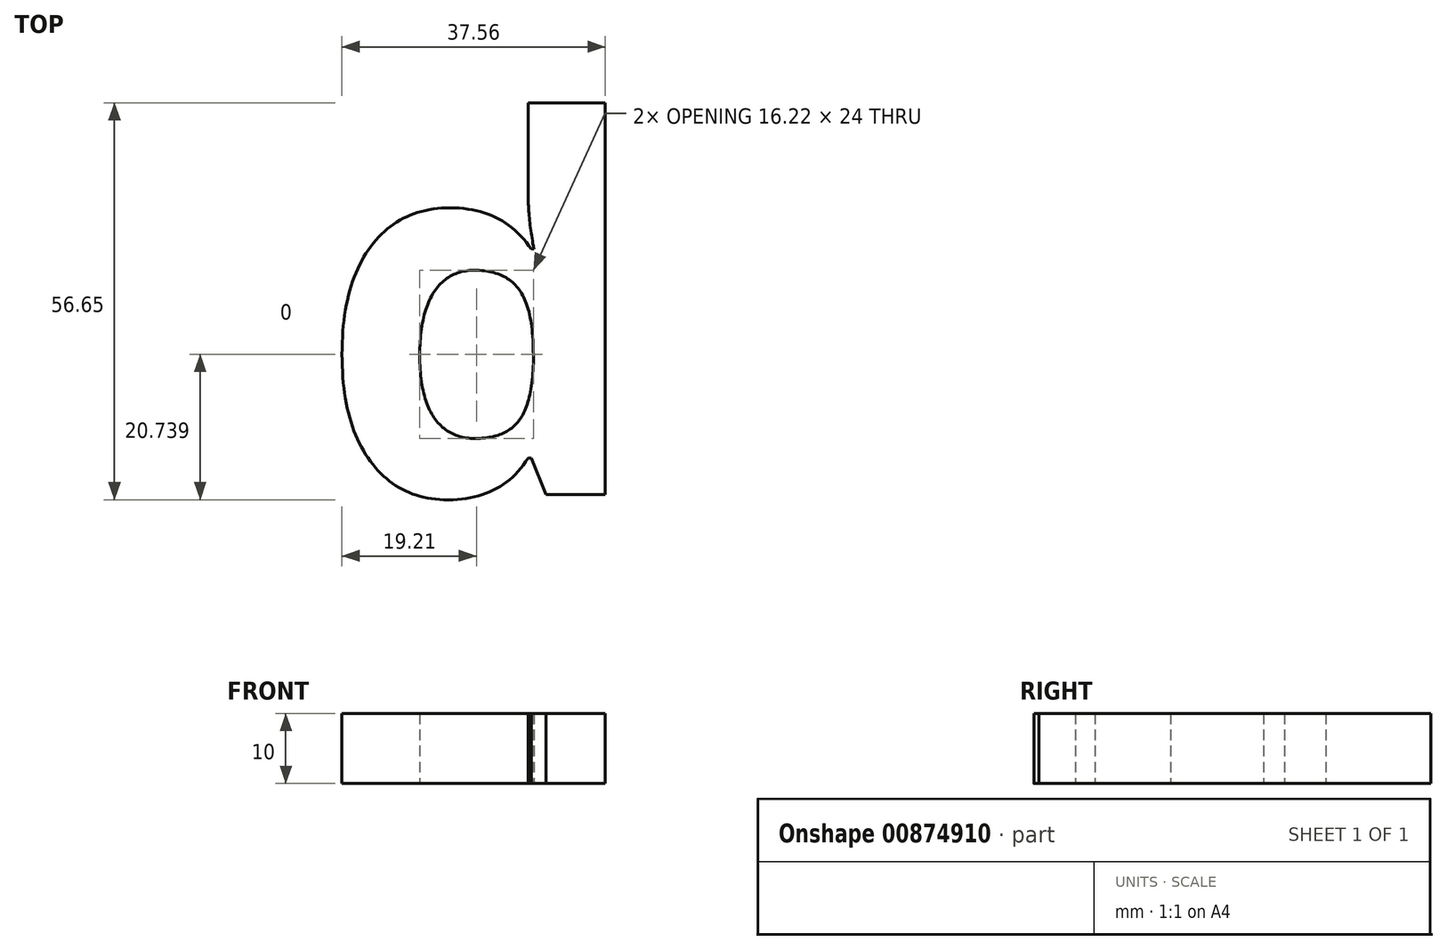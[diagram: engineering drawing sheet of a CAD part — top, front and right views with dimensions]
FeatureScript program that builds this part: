
annotation { "Feature Type Name" : "Feature", "Feature Type Description" : "" }
export const myFeature = defineFeature(function(context is Context, id is Id, definition is map)
    precondition{}
    {
        {
            var Q0;
            Q0=qCreatedBy(makeId("Top.planeOp"),FACE);
            var sketch = newSketch(context, id + "F0", { "sketchPlane" : qUnion([Q0])});
            skText(sketch, "E0", { "text": "d", "fontName": "OpenSans-Bold.ttf"});
            const initialGuessF0  = {"E0": [0, 0, 1, 0, 0.053]};
            skSetInitialGuess(sketch, initialGuessF0);
            skSolve(sketch);
        }
        {
            var Q0;
            Q0 = qSketchRegion(id + "F0", true);
            extrude(context, id + "F1", {"entities" : qUnion([Q0]), "depth" : 10 * mm, "offsetDistance" : 25 * mm});
        }
    });
